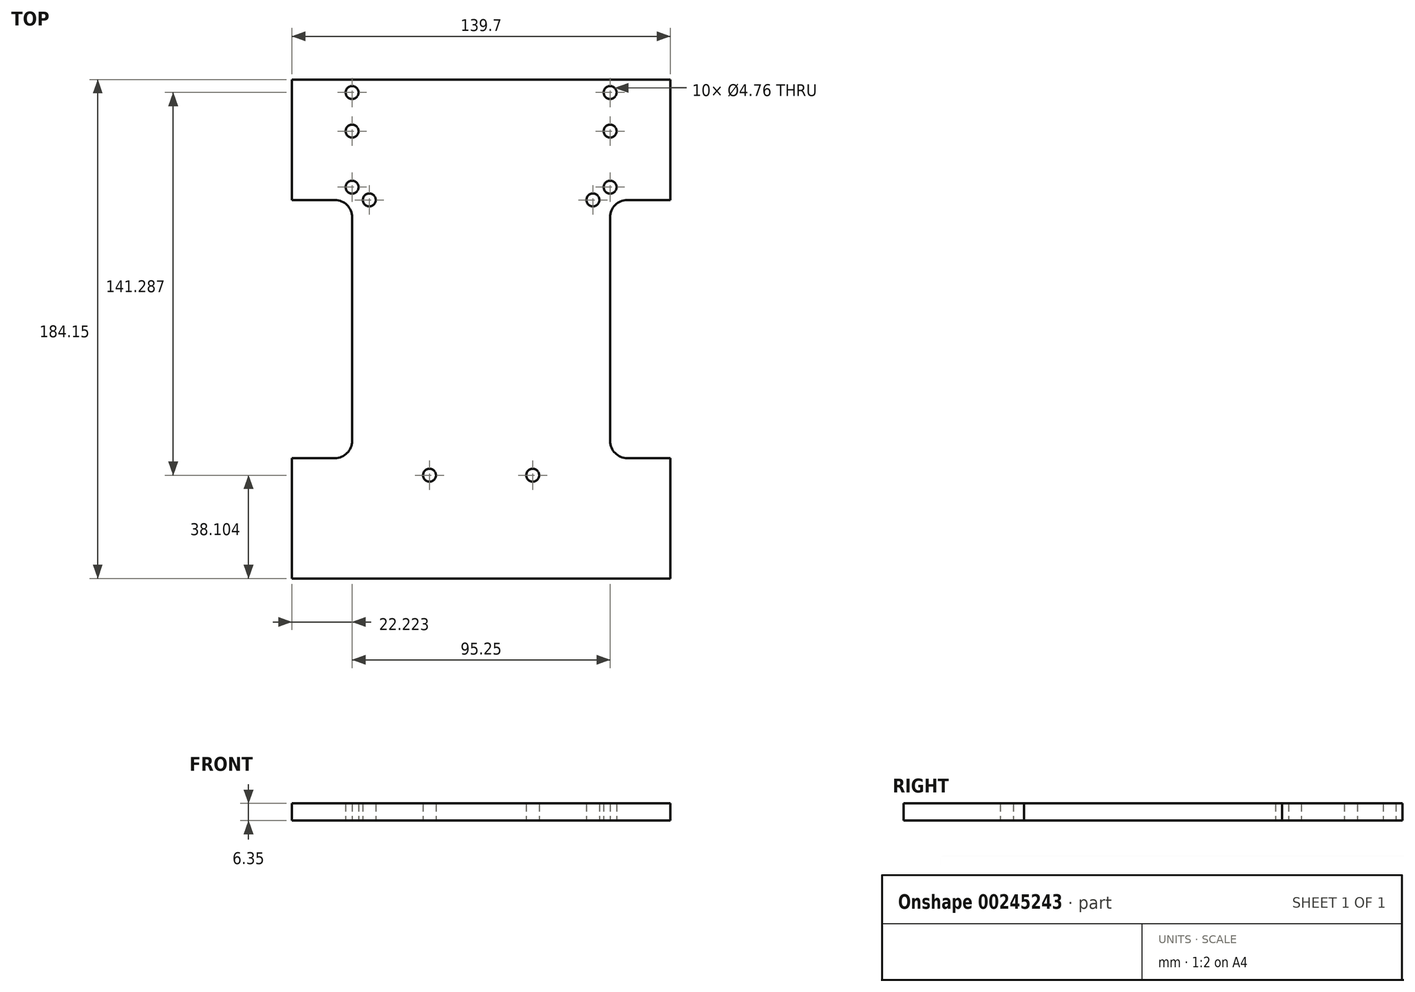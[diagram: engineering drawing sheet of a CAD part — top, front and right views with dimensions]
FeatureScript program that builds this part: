
annotation { "Feature Type Name" : "Feature", "Feature Type Description" : "" }
export const myFeature = defineFeature(function(context is Context, id is Id, definition is map)
    precondition{}
    {
        {
            var Q0;
            Q0=qCreatedBy(makeId("Top.planeOp"),FACE);
            var sketch = newSketch(context, id + "F0", { "sketchPlane" : qUnion([Q0])});
            skLineSegment(sketch, "E0", {"start": v(-62.34, 85.3) * mm, "end": v(77.36, 85.3) * mm});
            skLineSegment(sketch, "E1", {"start": v(77.36, 85.3) * mm, "end": v(77.36, 40.84) * mm});
            skLineSegment(sketch, "E2", {"start": v(77.36, 40.84) * mm, "end": v(61.48, 40.84) * mm});
            skLineSegment(sketch, "E3", {"start": v(55.13, 34.5) * mm, "end": v(55.13, -48.06) * mm});
            skLineSegment(sketch, "E4", {"start": v(61.48, -54.4) * mm, "end": v(77.36, -54.4) * mm});
            skLineSegment(sketch, "E5", {"start": v(77.36, -54.4) * mm, "end": v(77.36, -98.86) * mm});
            skLineSegment(sketch, "E6", {"start": v(77.36, -98.86) * mm, "end": v(-62.34, -98.86) * mm});
            skLineSegment(sketch, "E7", {"start": v(-62.34, -98.86) * mm, "end": v(-62.34, -54.4) * mm});
            skLineSegment(sketch, "E8", {"start": v(-62.34, -54.4) * mm, "end": v(-46.47, -54.4) * mm});
            skLineSegment(sketch, "E9", {"start": v(-40.12, -48.06) * mm, "end": v(-40.12, 34.5) * mm});
            skLineSegment(sketch, "E10", {"start": v(-46.47, 40.84) * mm, "end": v(-62.34, 40.84) * mm});
            skLineSegment(sketch, "E11", {"start": v(-62.34, 40.84) * mm, "end": v(-62.34, 85.3) * mm});
            skPoint(sketch, "E12.visualSharp", {"position": v(55.13, 40.84) * mm});
            skArc(sketch, "E12.filletArc", {"start": v(61.48, 40.84) * mm, "mid": v(57, 38.98) * mm, "end": v(55.13, 34.5) * mm});
            skPoint(sketch, "E13.visualSharp", {"position": v(55.13, -54.4) * mm});
            skArc(sketch, "E13.filletArc", {"start": v(55.13, -48.06) * mm, "mid": v(57, -52.55) * mm, "end": v(61.48, -54.4) * mm});
            skPoint(sketch, "E14.visualSharp", {"position": v(-40.12, -54.4) * mm});
            skArc(sketch, "E14.filletArc", {"start": v(-46.47, -54.4) * mm, "mid": v(-41.98, -52.55) * mm, "end": v(-40.12, -48.06) * mm});
            skPoint(sketch, "E15.visualSharp", {"position": v(-40.12, 40.84) * mm});
            skArc(sketch, "E15.filletArc", {"start": v(-40.12, 34.5) * mm, "mid": v(-41.98, 38.98) * mm, "end": v(-46.47, 40.84) * mm});
            skCircle(sketch, "E16", {"center": v(-40.12, 80.53) * mm, "radius": 2.38 * mm});
            skCircle(sketch, "E17", {"center": v(55.13, 80.53) * mm, "radius": 2.38 * mm});
            skCircle(sketch, "E18", {"center": v(55.13, 66.24) * mm, "radius": 2.38 * mm});
            skCircle(sketch, "E19", {"center": v(-40.12, 66.24) * mm, "radius": 2.38 * mm});
            skCircle(sketch, "E20", {"center": v(55.13, 45.6) * mm, "radius": 2.38 * mm});
            skCircle(sketch, "E21", {"center": v(-40.12, 45.6) * mm, "radius": 2.38 * mm});
            skLineSegment(sketch, "E22", {"start": v(-62.34, -60.76) * mm, "end": v(77.36, -60.76) * mm, "construction": true});
            skLineSegment(sketch, "E23", {"start": v(-40.12, 80.53) * mm, "end": v(-40.12, -98.86) * mm, "construction": true});
            skLineSegment(sketch, "E24", {"start": v(55.13, 80.53) * mm, "end": v(55.13, -98.86) * mm, "construction": true});
            skLineSegment(sketch, "E25", {"start": v(55.13, 80.53) * mm, "end": v(55.13, 85.3) * mm, "construction": true});
            skLineSegment(sketch, "E26", {"start": v(-40.12, 80.53) * mm, "end": v(-40.12, 85.3) * mm, "construction": true});
            skLineSegment(sketch, "E27", {"start": v(-11.54, -60.76) * mm, "end": v(-11.54, -98.86) * mm, "construction": true});
            skLineSegment(sketch, "E28", {"start": v(26.56, -60.76) * mm, "end": v(26.56, -98.86) * mm, "construction": true});
            skLineSegment(sketch, "E29", {"start": v(-62.34, -98.86) * mm, "end": v(-11.54, -98.86) * mm});
            skCircle(sketch, "E30", {"center": v(-11.54, -60.76) * mm, "radius": 2.38 * mm});
            skCircle(sketch, "E31", {"center": v(26.56, -60.76) * mm, "radius": 2.38 * mm});
            skLineSegment(sketch, "E32", {"start": v(-40.12, 40.84) * mm, "end": v(55.13, 40.84) * mm, "construction": true});
            skLineSegment(sketch, "E33", {"start": v(-33.77, -60.76) * mm, "end": v(-33.77, 40.84) * mm, "construction": true});
            skLineSegment(sketch, "E34", {"start": v(48.78, -60.76) * mm, "end": v(48.78, 40.84) * mm, "construction": true});
            skCircle(sketch, "E35", {"center": v(-33.77, 40.84) * mm, "radius": 2.38 * mm});
            skCircle(sketch, "E36", {"center": v(48.78, 40.84) * mm, "radius": 2.38 * mm});
            skSolve(sketch);
        }
        {
            var Q0;
            Q0 = qSketchRegion(id + "F0", true);
            extrude(context, id + "F1", {"entities" : qUnion([Q0]), "depth" : 6.35 * mm});
        }
    });
